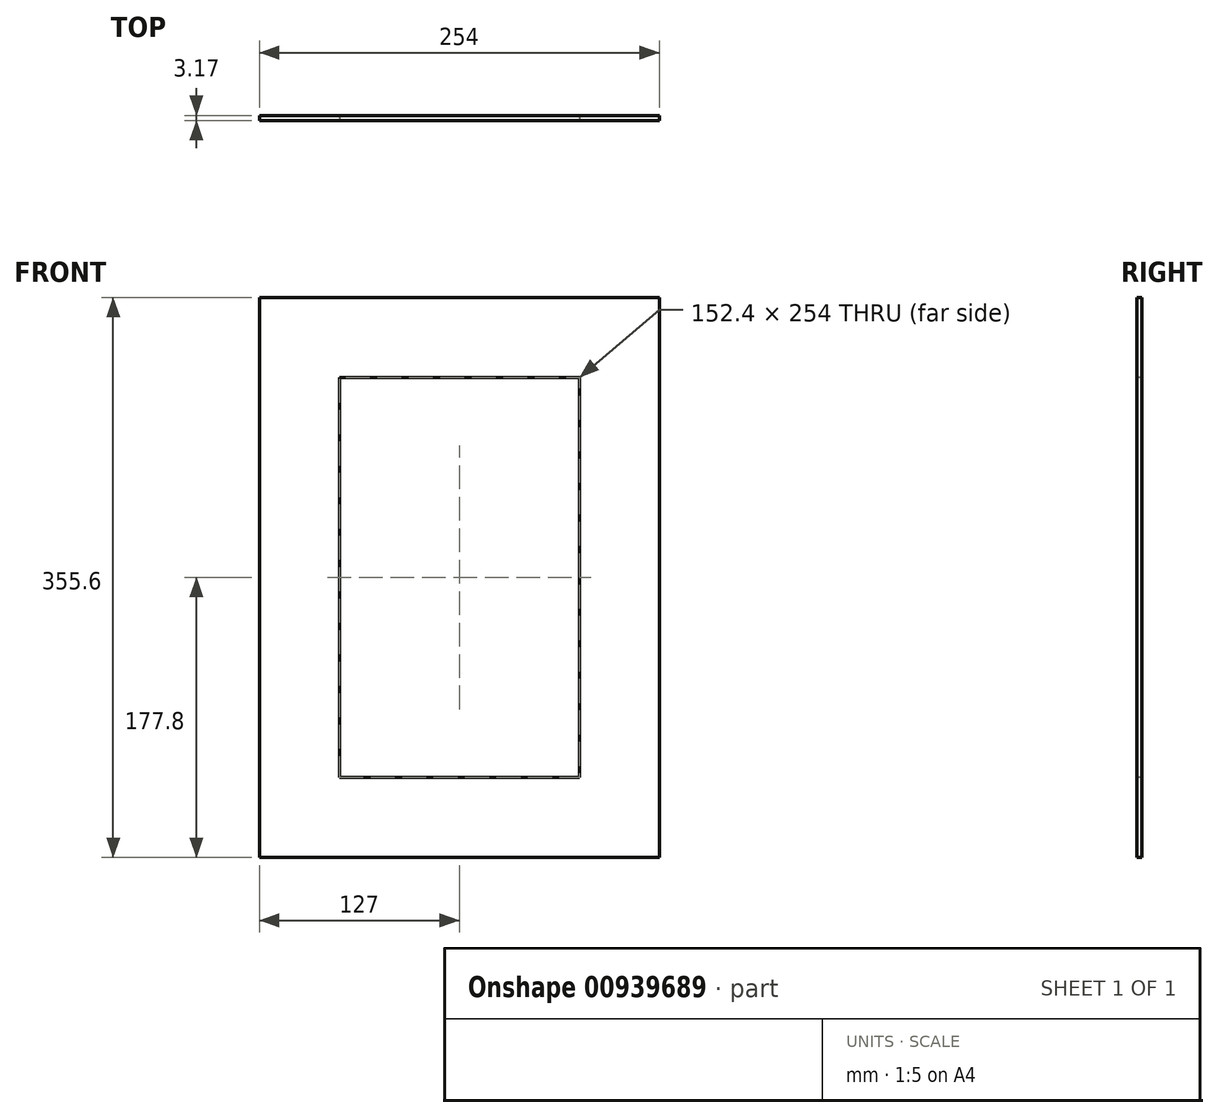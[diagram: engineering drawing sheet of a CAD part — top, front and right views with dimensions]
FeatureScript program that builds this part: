
annotation { "Feature Type Name" : "Feature", "Feature Type Description" : "" }
export const myFeature = defineFeature(function(context is Context, id is Id, definition is map)
    precondition{}
    {
        {
            var Q0;
            Q0=qCreatedBy(makeId("Front.planeOp"),FACE);
            var sketch = newSketch(context, id + "F0", { "sketchPlane" : qUnion([Q0])});
            skLineSegment(sketch, "E0.bottom", {"start": v(0, 0) * mm, "end": v(-254, 0) * mm});
            skLineSegment(sketch, "E0.top", {"start": v(0, 355.6) * mm, "end": v(-254, 355.6) * mm});
            skLineSegment(sketch, "E0.left", {"start": v(0, 0) * mm, "end": v(0, 355.6) * mm});
            skLineSegment(sketch, "E0.right", {"start": v(-254, 0) * mm, "end": v(-254, 355.6) * mm});
            skLineSegment(sketch, "E1.bottom", {"start": v(-50.8, 50.8) * mm, "end": v(-203.2, 50.8) * mm});
            skLineSegment(sketch, "E1.top", {"start": v(-50.8, 304.8) * mm, "end": v(-203.2, 304.8) * mm});
            skLineSegment(sketch, "E1.left", {"start": v(-50.8, 50.8) * mm, "end": v(-50.8, 304.8) * mm});
            skLineSegment(sketch, "E1.right", {"start": v(-203.2, 50.8) * mm, "end": v(-203.2, 304.8) * mm});
            skSolve(sketch);
        }
        {
            var Q0;
            Q0 = qSketchRegion(id + "F0", true);
            extrude(context, id + "F1", {"entities" : qUnion([Q0]), "oppositeDirection" : true, "depth" : 3.17 * mm, "offsetDistance" : 25.4 * mm});
        }
    });
